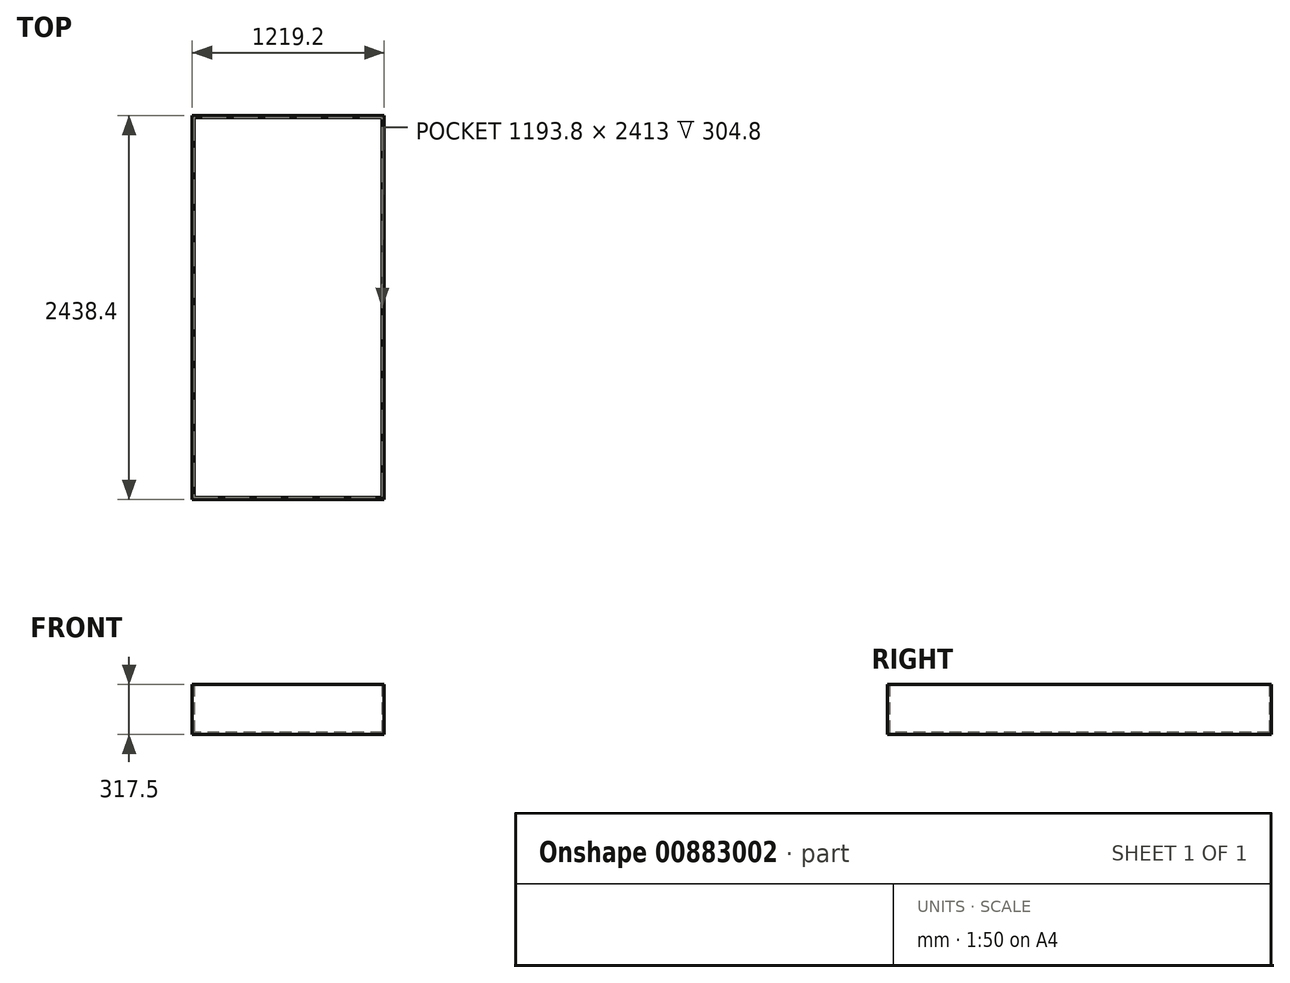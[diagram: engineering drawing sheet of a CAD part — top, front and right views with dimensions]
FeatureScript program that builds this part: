
annotation { "Feature Type Name" : "Feature", "Feature Type Description" : "" }
export const myFeature = defineFeature(function(context is Context, id is Id, definition is map)
    precondition{}
    {
        {
            var Q0;
            Q0=qCreatedBy(makeId("Top.planeOp"),FACE);
            var sketch = newSketch(context, id + "F0", { "sketchPlane" : qUnion([Q0])});
            skLineSegment(sketch, "E0.bottom", {"start": v(-41.55, -11.71) * mm, "end": v(1177.65, -11.71) * mm});
            skLineSegment(sketch, "E0.top", {"start": v(-41.55, 2426.69) * mm, "end": v(1177.65, 2426.69) * mm});
            skLineSegment(sketch, "E0.left", {"start": v(-41.55, -11.71) * mm, "end": v(-41.55, 2426.69) * mm});
            skLineSegment(sketch, "E0.right", {"start": v(1177.65, -11.71) * mm, "end": v(1177.65, 2426.69) * mm});
            skSolve(sketch);
        }
        {
            var Q0;
            Q0 = qSketchRegion(id + "F0", true);
            extrude(context, id + "F1", {"entities" : qUnion([Q0]), "depth" : 12.7 * mm, "offsetDistance" : 25.4 * mm});
        }
        {
            var Q0;
            Q0=makeQuery(id+"F1.opExtrude","CAP_FACE",FACE,{"disambiguationData":[OSD([sQuery(id+"F0.wireOp",EDGE,"E0.bottom"),sQuery(id+"F0.wireOp",EDGE,"E0.top"),sQuery(id+"F0.wireOp",EDGE,"E0.left"),sQuery(id+"F0.wireOp",EDGE,"E0.right")])],"isStart":false});
            var sketch = newSketch(context, id + "F2", { "sketchPlane" : qUnion([Q0])});
            skLineSegment(sketch, "E1", {"start": v(1177.65, 2426.69) * mm, "end": v(1164.95, 2426.69) * mm});
            skLineSegment(sketch, "E2", {"start": v(1164.95, 2426.69) * mm, "end": v(1164.95, -11.71) * mm});
            skLineSegment(sketch, "E3", {"start": v(1164.95, -11.71) * mm, "end": v(1177.65, -11.71) * mm});
            skLineSegment(sketch, "E4", {"start": v(1177.65, -11.71) * mm, "end": v(1177.65, 2426.69) * mm});
            skSolve(sketch);
        }
        {
            var Q0;
            Q0 = qSketchRegion(id + "F2", true);
            extrude(context, id + "F3", {"entities" : qUnion([Q0]), "operationType" : NewBodyOperationType.ADD, "depth" : 304.8 * mm, "offsetDistance" : 25.4 * mm});
        }
        {
            var Q0;
            Q0=makeQuery(id+"F1.opExtrude","CAP_FACE",FACE,{"disambiguationData":[OSD([sQuery(id+"F0.wireOp",EDGE,"E0.bottom"),sQuery(id+"F0.wireOp",EDGE,"E0.top"),sQuery(id+"F0.wireOp",EDGE,"E0.left"),sQuery(id+"F0.wireOp",EDGE,"E0.right")])],"isStart":false});
            var sketch = newSketch(context, id + "F4", { "sketchPlane" : qUnion([Q0])});
            skLineSegment(sketch, "E5", {"start": v(-41.55, 2426.69) * mm, "end": v(-28.85, 2426.69) * mm});
            skLineSegment(sketch, "E6", {"start": v(-28.85, 2426.69) * mm, "end": v(-28.85, -11.71) * mm});
            skLineSegment(sketch, "E7", {"start": v(-28.85, -11.71) * mm, "end": v(-41.55, -11.71) * mm});
            skLineSegment(sketch, "E8", {"start": v(-41.55, -11.71) * mm, "end": v(-41.55, 2426.69) * mm});
            skSolve(sketch);
        }
        {
            var Q0;
            Q0 = qSketchRegion(id + "F4", true);
            extrude(context, id + "F5", {"entities" : qUnion([Q0]), "operationType" : NewBodyOperationType.ADD, "depth" : 304.8 * mm, "offsetDistance" : 25.4 * mm});
        }
        {
            var Q0;
            Q0=makeQuery(id+"F1.opExtrude","CAP_FACE",FACE,{"disambiguationData":[OSD([sQuery(id+"F0.wireOp",EDGE,"E0.bottom"),sQuery(id+"F0.wireOp",EDGE,"E0.top"),sQuery(id+"F0.wireOp",EDGE,"E0.left"),sQuery(id+"F0.wireOp",EDGE,"E0.right")])],"isStart":false});
            var sketch = newSketch(context, id + "F6", { "sketchPlane" : qUnion([Q0])});
            skLineSegment(sketch, "E9", {"start": v(1164.95, 2426.69) * mm, "end": v(1164.95, 2413.99) * mm});
            skLineSegment(sketch, "E10", {"start": v(1164.95, 2413.99) * mm, "end": v(-28.85, 2413.99) * mm});
            skLineSegment(sketch, "E11", {"start": v(-28.85, 2413.99) * mm, "end": v(-28.85, 2426.69) * mm});
            skLineSegment(sketch, "E12", {"start": v(-28.85, 2426.69) * mm, "end": v(1164.95, 2426.69) * mm});
            skSolve(sketch);
        }
        {
            var Q0;
            Q0 = qSketchRegion(id + "F6", true);
            extrude(context, id + "F7", {"entities" : qUnion([Q0]), "operationType" : NewBodyOperationType.ADD, "depth" : 304.8 * mm, "offsetDistance" : 25.4 * mm});
        }
        {
            var Q0;
            Q0=makeQuery(id+"F1.opExtrude","CAP_FACE",FACE,{"disambiguationData":[OSD([sQuery(id+"F0.wireOp",EDGE,"E0.bottom"),sQuery(id+"F0.wireOp",EDGE,"E0.top"),sQuery(id+"F0.wireOp",EDGE,"E0.left"),sQuery(id+"F0.wireOp",EDGE,"E0.right")])],"isStart":false});
            var sketch = newSketch(context, id + "F8", { "sketchPlane" : qUnion([Q0])});
            skLineSegment(sketch, "E13", {"start": v(1164.95, -11.71) * mm, "end": v(1164.95, 0.99) * mm});
            skLineSegment(sketch, "E14", {"start": v(1164.95, 0.99) * mm, "end": v(-28.85, 0.99) * mm});
            skLineSegment(sketch, "E15", {"start": v(-28.85, 0.99) * mm, "end": v(-28.85, -11.71) * mm});
            skLineSegment(sketch, "E16", {"start": v(-28.85, -11.71) * mm, "end": v(1164.95, -11.71) * mm});
            skSolve(sketch);
        }
        {
            var Q0;
            Q0 = qSketchRegion(id + "F8", true);
            extrude(context, id + "F9", {"entities" : qUnion([Q0]), "operationType" : NewBodyOperationType.ADD, "depth" : 304.8 * mm, "offsetDistance" : 25.4 * mm});
        }
    });
